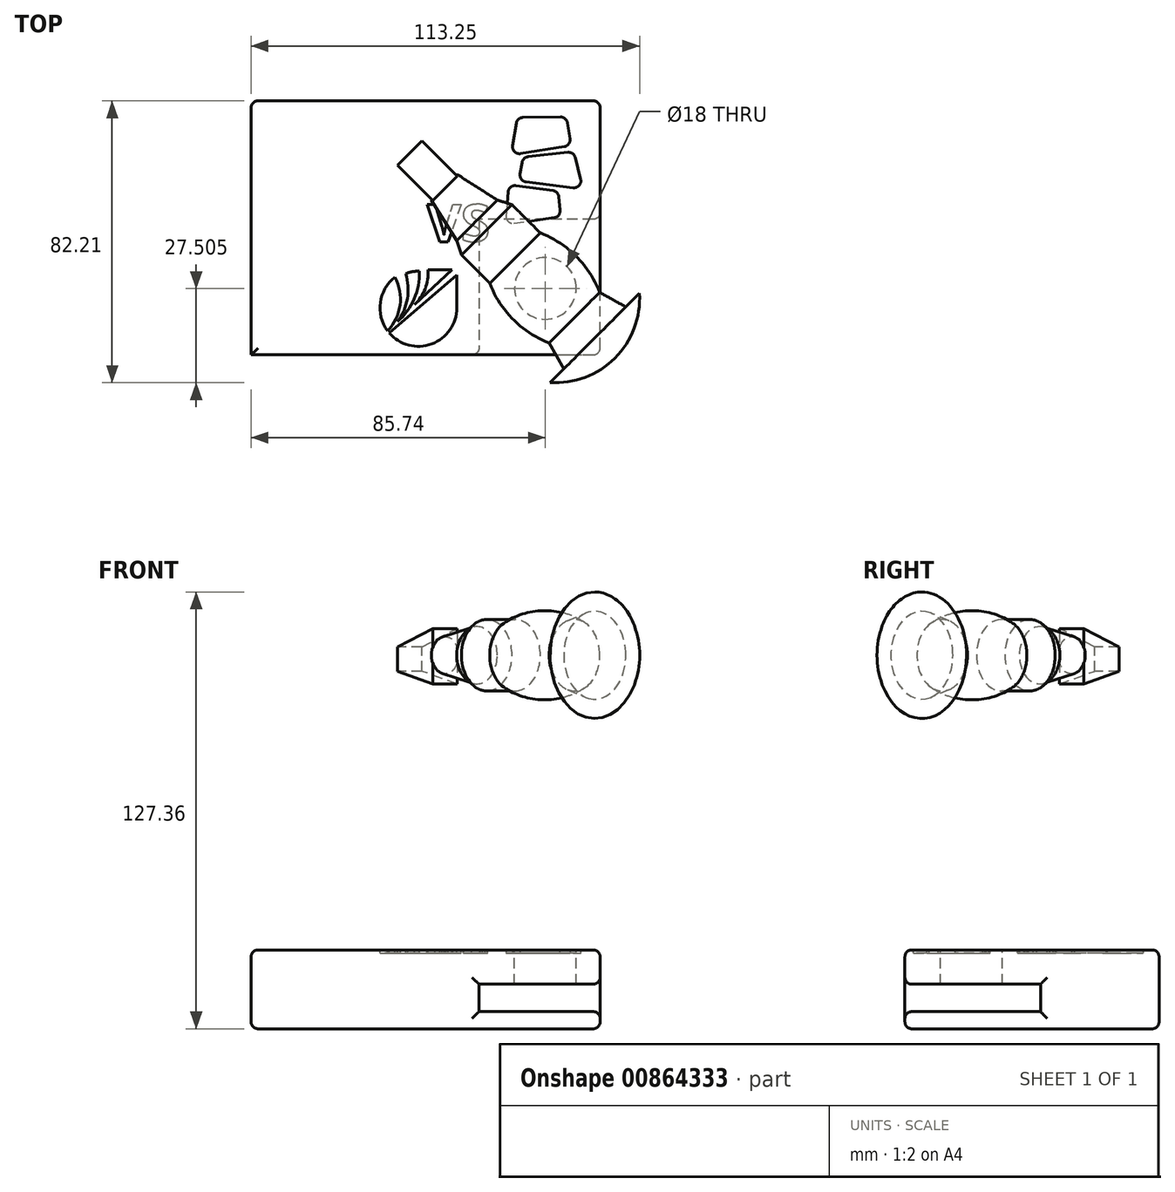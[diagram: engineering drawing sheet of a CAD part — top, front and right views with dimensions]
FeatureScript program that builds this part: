
annotation { "Feature Type Name" : "Feature", "Feature Type Description" : "" }
export const myFeature = defineFeature(function(context is Context, id is Id, definition is map)
    precondition{}
    {
        {
            var Q0;
            Q0=qCreatedBy(makeId("Top.planeOp"),FACE);
            cPlane(context, id + "F0", {"entities" : qUnion([Q0]), "cplaneType" : CPlaneType.OFFSET, "offset" : 36 * mm, "oppositeDirection" : true, "width" : 150 * mm, "height" : 150 * mm});
        }
        {
            var Q0;
            Q0=qCreatedBy(makeId("Top.planeOp"),FACE);
            cPlane(context, id + "F1", {"entities" : qUnion([Q0]), "cplaneType" : CPlaneType.OFFSET, "offset" : 40 * mm, "width" : 150 * mm, "height" : 150 * mm});
        }
        {
            var Q0;
            Q0=qCreatedBy(makeId("Front.planeOp"),FACE);
            var sketch = newSketch(context, id + "F2", { "sketchPlane" : qUnion([Q0])});
            skLineSegment(sketch, "E0", {"start": v(0, 86.74) * mm, "end": v(0, -86.44) * mm});
            skSolve(sketch);
        }
        {
            var Q0;
            Q0=sQuery(id+"F2.wireOp",EDGE,"E0");
            var Q1;
            Q1=qCreatedBy(makeId("Front.planeOp"),FACE);
            cPlane(context, id + "F3", {"entities" : qUnion([Q0, Q1]), "cplaneType" : CPlaneType.LINE_ANGLE, "offset" : 25 * mm, "angle" : 45 * degree, "width" : 150 * mm, "height" : 150 * mm});
        }
        {
            var Q0;
            Q0=qCreatedBy(id+"F3.planeOp",FACE);
            cPlane(context, id + "F4", {"entities" : qUnion([Q0]), "cplaneType" : CPlaneType.OFFSET, "offset" : 25 * mm, "width" : 150 * mm, "height" : 150 * mm});
        }
        {
            var Q0;
            Q0=qCreatedBy(id+"F4.planeOp",FACE);
            var sketch = newSketch(context, id + "F5", { "sketchPlane" : qUnion([Q0])});
            skLineSegment(sketch, "E1", {"start": v(-75.39, 49.92) * mm, "end": v(-11.92, 49.92) * mm});
            skLineSegment(sketch, "E2", {"start": v(-11.92, 49.92) * mm, "end": v(-11.92, 55.3) * mm});
            skLineSegment(sketch, "E3", {"start": v(-73.9, 62.7) * mm, "end": v(-73.9, 68.36) * mm});
            skLineSegment(sketch, "E4", {"start": v(-29.35, 60.33) * mm, "end": v(-41.03, 60.33) * mm});
            skArc(sketch, "E5", {"start": v(-41.03, 60.33) * mm, "mid": v(-53.27, 62.93) * mm, "end": v(-65.52, 60.33) * mm});
            skLineSegment(sketch, "E6", {"start": v(-65.52, 60.33) * mm, "end": v(-73.9, 62.7) * mm});
            skLineSegment(sketch, "E7", {"start": v(-11.92, 55.3) * mm, "end": v(-25.37, 58.26) * mm});
            skLineSegment(sketch, "E8", {"start": v(-25.37, 58.26) * mm, "end": v(-29.35, 60.33) * mm});
            skArc(sketch, "E9", {"start": v(-73.9, 68.36) * mm, "mid": v(-80.03, 60.03) * mm, "end": v(-82.2, 49.92) * mm});
            skLineSegment(sketch, "E10", {"start": v(-75.39, 49.92) * mm, "end": v(-82.2, 49.92) * mm});
            skSolve(sketch);
        }
        {
            var Q0;
            Q0=qSketchRegion(id+"F5",true);
            var Q1;
            Q1=sQuery(id+"F5.wireOp",EDGE,"E1");
            revolve(context, id + "F6", {"surfaceOperationType" : NewSurfaceOperationType.NEW, "entities" : qUnion([Q0]), "axis" : qUnion([Q1]), "revolveType" : RevolveType.FULL});
        }
        {
            var Q0;
            Q0=qCreatedBy(id+"F4.planeOp",FACE);
            var sketch = newSketch(context, id + "F7", { "sketchPlane" : qUnion([Q0])});
            skLineSegment(sketch, "E11", {"start": v(-12.2, 57.73) * mm, "end": v(-12.2, 41.5) * mm});
            skLineSegment(sketch, "E12", {"start": v(-12.2, 41.5) * mm, "end": v(2.33, 45.24) * mm});
            skLineSegment(sketch, "E13", {"start": v(2.33, 45.24) * mm, "end": v(2.33, 52.3) * mm});
            skLineSegment(sketch, "E14", {"start": v(2.33, 52.3) * mm, "end": v(-12.2, 57.73) * mm});
            skSolve(sketch);
        }
        {
            var Q0;
            Q0=qSketchRegion(id+"F7",true);
            extrude(context, id + "F8", {"entities" : qUnion([Q0]), "operationType" : NewBodyOperationType.ADD, "depth" : 5 * mm, "offsetDistance" : 25 * mm});
        }
        {
            var Q0;
            Q0=qSketchRegion(id+"F7",true);
            extrude(context, id + "F9", {"entities" : qUnion([Q0]), "operationType" : NewBodyOperationType.ADD, "oppositeDirection" : true, "depth" : 5 * mm, "offsetDistance" : 25 * mm});
        }
        {
            var Q0;
            Q0=qCreatedBy(id+"F0.planeOp",FACE);
            var sketch = newSketch(context, id + "F10", { "sketchPlane" : qUnion([Q0])});
            skCircle(sketch, "E15", {"center": v(55.51, -20.16) * mm, "radius": 7.65 * mm});
            skSolve(sketch);
        }
        {
            var Q0;
            Q0=qCreatedBy(id+"F0.planeOp",FACE);
            var sketch = newSketch(context, id + "F11", { "sketchPlane" : qUnion([Q0])});
            skLineSegment(sketch, "E16.bottom", {"start": v(-30.23, -39.51) * mm, "end": v(71.47, -39.51) * mm});
            skLineSegment(sketch, "E16.top", {"start": v(-30.23, 34.55) * mm, "end": v(71.47, 34.55) * mm});
            skLineSegment(sketch, "E16.left", {"start": v(-30.23, -39.51) * mm, "end": v(-30.23, 34.55) * mm});
            skLineSegment(sketch, "E16.right", {"start": v(71.47, -39.51) * mm, "end": v(71.47, 34.55) * mm});
            skCircle(sketch, "E17", {"center": v(55.51, -20.16) * mm, "radius": 9 * mm});
            skSolve(sketch);
        }
        {
            var Q0;
            Q0=qSketchRegion(id+"F11",true);
            extrude(context, id + "F12", {"entities" : qUnion([Q0]), "operationType" : NewBodyOperationType.ADD, "oppositeDirection" : true, "depth" : 10 * mm, "offsetDistance" : 25 * mm});
        }
        {
            var Q0;
            Q0=makeQuery(id+"F12.opExtrude","CAP_FACE",FACE,{"disambiguationData":[OSD([sQuery(id+"F11.wireOp",EDGE,"E16.bottom"),sQuery(id+"F11.wireOp",EDGE,"E16.top"),sQuery(id+"F11.wireOp",EDGE,"E16.left"),sQuery(id+"F11.wireOp",EDGE,"E16.right"),sQuery(id+"F11.wireOp",EDGE,"E17")])],"isStart":false});
            cPlane(context, id + "F13", {"entities" : qUnion([Q0]), "cplaneType" : CPlaneType.OFFSET, "offset" : 1 * mm, "width" : 150 * mm, "height" : 150 * mm});
        }
        {
            var Q0;
            Q0=makeQuery(id+"F12.opExtrude","CAP_FACE",FACE,{"disambiguationData":[OSD([sQuery(id+"F11.wireOp",EDGE,"E16.bottom"),sQuery(id+"F11.wireOp",EDGE,"E16.top"),sQuery(id+"F11.wireOp",EDGE,"E16.left"),sQuery(id+"F11.wireOp",EDGE,"E16.right"),sQuery(id+"F11.wireOp",EDGE,"E17")])],"isStart":false});
            var sketch = newSketch(context, id + "F14", { "sketchPlane" : qUnion([Q0])});
            skLineSegment(sketch, "E18", {"start": v(71.47, -34.55) * mm, "end": v(71.47, 0) * mm});
            skLineSegment(sketch, "E19", {"start": v(71.47, 0) * mm, "end": v(36.17, 0) * mm});
            skLineSegment(sketch, "E20", {"start": v(-30.23, -34.55) * mm, "end": v(71.47, -34.55) * mm});
            skLineSegment(sketch, "E21", {"start": v(-30.23, -34.55) * mm, "end": v(-30.23, 0) * mm});
            skLineSegment(sketch, "E22", {"start": v(36.17, 0) * mm, "end": v(36.17, 39.51) * mm});
            skLineSegment(sketch, "E23", {"start": v(36.17, 39.51) * mm, "end": v(-30.23, 39.51) * mm});
            skLineSegment(sketch, "E24", {"start": v(-30.23, 39.51) * mm, "end": v(-30.23, 0) * mm});
            skSolve(sketch);
        }
        {
            var Q0;
            Q0=makeQuery(id+"F14.imprint","IMPRINT",FACE,{"disambiguationData":[TD([[makeQuery(id+"F14.imprint","IMPRINT",EDGE,{"derivedFrom":sQuery(id+"F14.wireOp",EDGE,"E18")}),-1.0]])]});
            extrude(context, id + "F15", {"entities" : qUnion([Q0]), "operationType" : NewBodyOperationType.ADD, "depth" : 8 * mm, "offsetDistance" : 25 * mm});
        }
        {
            var Q0;
            Q0=makeQuery(id+"F15.opExtrude","CAP_FACE",FACE,{"disambiguationData":[OSD([sQuery(id+"F14.wireOp",EDGE,"E18"),sQuery(id+"F14.wireOp",EDGE,"E19"),sQuery(id+"F14.wireOp",EDGE,"E20"),sQuery(id+"F14.wireOp",EDGE,"iN0juFn1-ICa9-M7KA-fJVA-QljqQybucplU"),sQuery(id+"F14.wireOp",EDGE,"E21")])],"isStart":false});
            var sketch = newSketch(context, id + "F16", { "sketchPlane" : qUnion([Q0])});
            skLineSegment(sketch, "E25.bottom", {"start": v(-30.23, -34.55) * mm, "end": v(71.47, -34.55) * mm});
            skLineSegment(sketch, "E25.top", {"start": v(-30.23, 39.51) * mm, "end": v(71.47, 39.51) * mm});
            skLineSegment(sketch, "E25.left", {"start": v(-30.23, -34.55) * mm, "end": v(-30.23, 39.51) * mm});
            skLineSegment(sketch, "E25.right", {"start": v(71.47, -34.55) * mm, "end": v(71.47, 39.51) * mm});
            skSolve(sketch);
        }
        {
            var Q0;
            Q0=qSketchRegion(id+"F16",true);
            extrude(context, id + "F17", {"entities" : qUnion([Q0]), "operationType" : NewBodyOperationType.ADD, "depth" : 5 * mm, "offsetDistance" : 25 * mm});
        }
        {
            var Q0;
            Q0=makeQuery(id+"F12.opExtrude","CAP_FACE",FACE,{"disambiguationData":[OSD([sQuery(id+"F11.wireOp",EDGE,"E16.bottom"),sQuery(id+"F11.wireOp",EDGE,"E16.top"),sQuery(id+"F11.wireOp",EDGE,"E16.left"),sQuery(id+"F11.wireOp",EDGE,"E16.right"),sQuery(id+"F11.wireOp",EDGE,"E17")])],"isStart":true});
            var sketch = newSketch(context, id + "F18", { "sketchPlane" : qUnion([Q0])});
            skLineSegment(sketch, "E26.bottom", {"start": v(65.5, -22.08) * mm, "end": v(62.22, -22.08) * mm});
            skLineSegment(sketch, "E26.top", {"start": v(65.5, -21.47) * mm, "end": v(62.22, -21.47) * mm});
            skLineSegment(sketch, "E26.left", {"start": v(65.5, -22.08) * mm, "end": v(65.5, -21.47) * mm});
            skLineSegment(sketch, "E26.right", {"start": v(62.22, -22.08) * mm, "end": v(62.22, -21.47) * mm});
            skSolve(sketch);
        }
        {
            var Q0;
            Q0=makeQuery(id+"FpY5HfDL9gUgUrJ_86.boolean.opBoolean","MERGE",FACE,{"derivedFrom":[makeQuery(id+"F12.opExtrude","CAP_FACE",FACE,{"disambiguationData":[OSD([sQuery(id+"F11.wireOp",EDGE,"E16.bottom"),sQuery(id+"F11.wireOp",EDGE,"E16.top"),sQuery(id+"F11.wireOp",EDGE,"E16.left"),sQuery(id+"F11.wireOp",EDGE,"E16.right"),sQuery(id+"F11.wireOp",EDGE,"E17")])],"isStart":true}),makeQuery(id+"FpY5HfDL9gUgUrJ_86.opExtrude","CAP_FACE",FACE,{"disambiguationData":[OSD([sQuery(id+"F18.wireOp",EDGE,"E26.bottom"),sQuery(id+"F18.wireOp",EDGE,"E26.top"),sQuery(id+"F18.wireOp",EDGE,"E26.left"),sQuery(id+"F18.wireOp",EDGE,"E26.right")])],"isStart":true})]});
            var sketch = newSketch(context, id + "F19", { "sketchPlane" : qUnion([Q0])});
            skLineSegment(sketch, "E27", {"start": v(47.35, 29.69) * mm, "end": v(45.56, 18.71) * mm});
            skLineSegment(sketch, "E28", {"start": v(45.56, 18.71) * mm, "end": v(63, 21.5) * mm});
            skLineSegment(sketch, "E29", {"start": v(63, 21.5) * mm, "end": v(61.68, 29.86) * mm});
            skLineSegment(sketch, "E30", {"start": v(61.68, 29.86) * mm, "end": v(47.35, 29.69) * mm});
            skLineSegment(sketch, "E31", {"start": v(48.97, 18.09) * mm, "end": v(47.85, 11.15) * mm});
            skLineSegment(sketch, "E32", {"start": v(47.85, 11.15) * mm, "end": v(66.52, 8.87) * mm});
            skLineSegment(sketch, "E33", {"start": v(63.83, 19.72) * mm, "end": v(48.97, 18.09) * mm});
            skLineSegment(sketch, "E34", {"start": v(63.83, 19.72) * mm, "end": v(66.52, 8.87) * mm});
            skLineSegment(sketch, "E35", {"start": v(44.9, 10.13) * mm, "end": v(43.84, -1.5) * mm});
            skLineSegment(sketch, "E36", {"start": v(43.84, -1.5) * mm, "end": v(59.99, 0.74) * mm});
            skLineSegment(sketch, "E37", {"start": v(59.3, 8.18) * mm, "end": v(44.9, 10.13) * mm});
            skLineSegment(sketch, "E38", {"start": v(59.3, 8.18) * mm, "end": v(59.99, 0.74) * mm});
            skSolve(sketch);
        }
        {
            var Q0;
            Q0=qSketchRegion(id+"F19",true);
            extrude(context, id + "F20", {"entities" : qUnion([Q0]), "operationType" : NewBodyOperationType.REMOVE, "oppositeDirection" : true, "depth" : 1 * mm, "offsetDistance" : 25 * mm});
        }
        {
            var Q0;
            Q0=makeQuery(id+"F20.boolean.opBoolean","COPY",EDGE,{"derivedFrom":makeQuery(id+"F20.opExtrude","SWEPT_EDGE",EDGE,{"disambiguationData":[OSD([sQuery(id+"F19.wireOp",EDGE,"E36"),sQuery(id+"F19.wireOp",EDGE,"E38")])]})});
            var Q1;
            Q1=makeQuery(id+"F20.boolean.opBoolean","COPY",EDGE,{"derivedFrom":makeQuery(id+"F20.opExtrude","SWEPT_EDGE",EDGE,{"disambiguationData":[OSD([sQuery(id+"F19.wireOp",EDGE,"E37"),sQuery(id+"F19.wireOp",EDGE,"E38")])]})});
            var Q2;
            Q2=makeQuery(id+"F20.boolean.opBoolean","COPY",EDGE,{"derivedFrom":makeQuery(id+"F20.opExtrude","SWEPT_EDGE",EDGE,{"disambiguationData":[OSD([sQuery(id+"F19.wireOp",EDGE,"E35"),sQuery(id+"F19.wireOp",EDGE,"E36")])]})});
            var Q3;
            Q3=makeQuery(id+"F20.boolean.opBoolean","COPY",EDGE,{"derivedFrom":makeQuery(id+"F20.opExtrude","SWEPT_EDGE",EDGE,{"disambiguationData":[OSD([sQuery(id+"F19.wireOp",EDGE,"E35"),sQuery(id+"F19.wireOp",EDGE,"E37")])]})});
            var Q4;
            Q4=makeQuery(id+"F20.boolean.opBoolean","COPY",EDGE,{"derivedFrom":makeQuery(id+"F20.opExtrude","SWEPT_EDGE",EDGE,{"disambiguationData":[OSD([sQuery(id+"F19.wireOp",EDGE,"E31"),sQuery(id+"F19.wireOp",EDGE,"E32")])]})});
            var Q5;
            Q5=makeQuery(id+"F20.boolean.opBoolean","COPY",EDGE,{"derivedFrom":makeQuery(id+"F20.opExtrude","SWEPT_EDGE",EDGE,{"disambiguationData":[OSD([sQuery(id+"F19.wireOp",EDGE,"E27"),sQuery(id+"F19.wireOp",EDGE,"E28")])]})});
            var Q6;
            Q6=makeQuery(id+"F20.boolean.opBoolean","COPY",EDGE,{"derivedFrom":makeQuery(id+"F20.opExtrude","SWEPT_EDGE",EDGE,{"disambiguationData":[OSD([sQuery(id+"F19.wireOp",EDGE,"E31"),sQuery(id+"F19.wireOp",EDGE,"E33")])]})});
            var Q7;
            Q7=makeQuery(id+"F20.boolean.opBoolean","COPY",EDGE,{"derivedFrom":makeQuery(id+"F20.opExtrude","SWEPT_EDGE",EDGE,{"disambiguationData":[OSD([sQuery(id+"F19.wireOp",EDGE,"E27"),sQuery(id+"F19.wireOp",EDGE,"E30")])]})});
            var Q8;
            Q8=makeQuery(id+"F20.boolean.opBoolean","COPY",EDGE,{"derivedFrom":makeQuery(id+"F20.opExtrude","SWEPT_EDGE",EDGE,{"disambiguationData":[OSD([sQuery(id+"F19.wireOp",EDGE,"E29"),sQuery(id+"F19.wireOp",EDGE,"E30")])]})});
            var Q9;
            Q9=makeQuery(id+"F20.boolean.opBoolean","COPY",EDGE,{"derivedFrom":makeQuery(id+"F20.opExtrude","SWEPT_EDGE",EDGE,{"disambiguationData":[OSD([sQuery(id+"F19.wireOp",EDGE,"E33"),sQuery(id+"F19.wireOp",EDGE,"E34")])]})});
            var Q10;
            Q10=makeQuery(id+"F20.boolean.opBoolean","COPY",EDGE,{"derivedFrom":makeQuery(id+"F20.opExtrude","SWEPT_EDGE",EDGE,{"disambiguationData":[OSD([sQuery(id+"F19.wireOp",EDGE,"E28"),sQuery(id+"F19.wireOp",EDGE,"E29")])]})});
            var Q11;
            Q11=makeQuery(id+"F20.boolean.opBoolean","COPY",EDGE,{"derivedFrom":makeQuery(id+"F20.opExtrude","SWEPT_EDGE",EDGE,{"disambiguationData":[OSD([sQuery(id+"F19.wireOp",EDGE,"E32"),sQuery(id+"F19.wireOp",EDGE,"E34")])]})});
            fillet(context, id + "F21", {"entities" : qUnion([Q0, Q1, Q2, Q3, Q4, Q5, Q6, Q7, Q8, Q9, Q10, Q11]), "radius" : 2 * mm, "tangentPropagation" : true, "allowEdgeOverflow" : false});
        }
        {
            var Q0;
            Q0=makeQuery(id+"FpY5HfDL9gUgUrJ_86.boolean.opBoolean","MERGE",FACE,{"derivedFrom":[makeQuery(id+"F12.opExtrude","CAP_FACE",FACE,{"disambiguationData":[OSD([sQuery(id+"F11.wireOp",EDGE,"E16.bottom"),sQuery(id+"F11.wireOp",EDGE,"E16.top"),sQuery(id+"F11.wireOp",EDGE,"E16.left"),sQuery(id+"F11.wireOp",EDGE,"E16.right"),sQuery(id+"F11.wireOp",EDGE,"E17")])],"isStart":true}),makeQuery(id+"FpY5HfDL9gUgUrJ_86.opExtrude","CAP_FACE",FACE,{"disambiguationData":[OSD([sQuery(id+"F18.wireOp",EDGE,"E26.bottom"),sQuery(id+"F18.wireOp",EDGE,"E26.top"),sQuery(id+"F18.wireOp",EDGE,"E26.left"),sQuery(id+"F18.wireOp",EDGE,"E26.right")])],"isStart":true})]});
            var sketch = newSketch(context, id + "F22", { "sketchPlane" : qUnion([Q0])});
            skArc(sketch, "E39", {"start": v(10.01, -33.1) * mm, "mid": v(22.42, -36.32) * mm, "end": v(29.75, -25.8) * mm});
            skLineSegment(sketch, "E40", {"start": v(29.75, -25.8) * mm, "end": v(29.75, -16.19) * mm});
            skLineSegment(sketch, "E41", {"start": v(29.75, -16.19) * mm, "end": v(18.53, -25.8) * mm});
            skLineSegment(sketch, "E42", {"start": v(10.01, -33.1) * mm, "end": v(18.53, -25.8) * mm});
            skLineSegment(sketch, "E43", {"start": v(28.26, -14.71) * mm, "end": v(21.29, -14.71) * mm});
            skLineSegment(sketch, "E44", {"start": v(28.26, -14.71) * mm, "end": v(17.39, -24.9) * mm});
            skArc(sketch, "E45", {"start": v(11.71, -16.9) * mm, "mid": v(7.42, -24.24) * mm, "end": v(9.53, -32.5) * mm});
            skArc(sketch, "E46", {"start": v(9.53, -32.5) * mm, "mid": v(13.18, -25.05) * mm, "end": v(11.71, -16.9) * mm});
            skArc(sketch, "E47", {"start": v(12.42, -29.83) * mm, "mid": v(15.32, -23.1) * mm, "end": v(14.8, -15.79) * mm});
            skArc(sketch, "E48", {"start": v(12.42, -29.83) * mm, "mid": v(17.27, -23.2) * mm, "end": v(18.83, -15.12) * mm});
            skArc(sketch, "E49", {"start": v(17.39, -24.9) * mm, "mid": v(20.5, -20.25) * mm, "end": v(21.29, -14.71) * mm});
            skArc(sketch, "E50", {"start": v(18.83, -15.12) * mm, "mid": v(16.78, -15.26) * mm, "end": v(14.8, -15.79) * mm});
            skText(sketch, "E51", { "text": "VS", "fontName": "OpenSans-Bold.ttf"});
            const initialGuessF22  = {"E51": [0.02102, -0.00654, 1, 0, 0.01097]};
            skSetInitialGuess(sketch, initialGuessF22);
            skSolve(sketch);
        }
        {
            var Q0;
            Q0=qSketchRegion(id+"F22",true);
            extrude(context, id + "F23", {"entities" : qUnion([Q0]), "operationType" : NewBodyOperationType.REMOVE, "oppositeDirection" : true, "depth" : 1 * mm, "offsetDistance" : 25 * mm});
        }
        {
            var Q0;
            Q0=makeQuery(id+"F12.opExtrude","CAP_EDGE",EDGE,{"disambiguationData":[OSD([sQuery(id+"F11.wireOp",EDGE,"E16.bottom")])],"isStart":true});
            var Q1;
            Q1=makeQuery(id+"F12.opExtrude","CAP_EDGE",EDGE,{"disambiguationData":[OSD([sQuery(id+"F11.wireOp",EDGE,"E16.right")])],"isStart":true});
            var Q2;
            Q2=makeQuery(id+"F12.opExtrude","SWEPT_EDGE",EDGE,{"disambiguationData":[OSD([sQuery(id+"F11.wireOp",EDGE,"E16.bottom"),sQuery(id+"F11.wireOp",EDGE,"E16.right")])]});
            var Q3;
            Q3=makeQuery(id+"F17.opExtrude","SWEPT_EDGE",EDGE,{"disambiguationData":[OSD([sQuery(id+"F16.wireOp",EDGE,"E25.top"),sQuery(id+"F16.wireOp",EDGE,"E25.right")])]});
            var Q4;
            Q4=makeQuery(id+"F17.opExtrude","CAP_EDGE",EDGE,{"disambiguationData":[OSD([sQuery(id+"F16.wireOp",EDGE,"E25.top")])],"isStart":true});
            var Q5;
            Q5=makeQuery(id+"F17.opExtrude","CAP_EDGE",EDGE,{"disambiguationData":[OSD([sQuery(id+"F16.wireOp",EDGE,"E25.right")])],"isStart":true});
            var Q6;
            Q6=makeQuery(id+"F15.opExtrude","SWEPT_EDGE",EDGE,{"disambiguationData":[OSD([sQuery(id+"F11.wireOp",EDGE,"E16.right"),sQuery(id+"F14.wireOp",EDGE,"E18"),sQuery(id+"F14.wireOp",EDGE,"E19")])]});
            var Q7;
            Q7=makeQuery(id+"F12.opExtrude","CAP_EDGE",EDGE,{"disambiguationData":[OSD([sQuery(id+"F11.wireOp",EDGE,"E16.right")])],"isStart":false});
            var Q8;
            Q8=makeQuery(id+"F12.opExtrude","CAP_EDGE",EDGE,{"disambiguationData":[OSD([sQuery(id+"F11.wireOp",EDGE,"E16.bottom")])],"isStart":false});
            var Q9;
            Q9=makeQuery(id+"F15.opExtrude","SWEPT_EDGE",EDGE,{"disambiguationData":[OSD([sQuery(id+"F11.wireOp",EDGE,"E16.bottom"),sQuery(id+"F14.wireOp",EDGE,"E22"),sQuery(id+"F14.wireOp",EDGE,"E23")])]});
            var Q10;
            Q10=makeQuery(id+"F17.opExtrude","CAP_EDGE",EDGE,{"disambiguationData":[OSD([sQuery(id+"F16.wireOp",EDGE,"E25.top")])],"isStart":false});
            var Q11;
            Q11=makeQuery(id+"F17.opExtrude","CAP_EDGE",EDGE,{"disambiguationData":[OSD([sQuery(id+"F16.wireOp",EDGE,"E25.right")])],"isStart":false});
            var Q12;
            Q12=makeQuery(id+"F17.opExtrude","CAP_EDGE",EDGE,{"disambiguationData":[OSD([sQuery(id+"F16.wireOp",EDGE,"E25.bottom")])],"isStart":false});
            var Q13;
            Q13=makeQuery(id+"F17.boolean.opBoolean","MERGE",EDGE,{"derivedFrom":[makeQuery(id+"F15.boolean.opBoolean","MERGE",EDGE,{"derivedFrom":[makeQuery(id+"F12.opExtrude","SWEPT_EDGE",EDGE,{"disambiguationData":[OSD([sQuery(id+"F11.wireOp",EDGE,"E16.top"),sQuery(id+"F11.wireOp",EDGE,"E16.right")])]}),makeQuery(id+"F15.opExtrude","SWEPT_EDGE",EDGE,{"disambiguationData":[OSD([sQuery(id+"F14.wireOp",EDGE,"E18"),sQuery(id+"F14.wireOp",EDGE,"E20")])]})]}),makeQuery(id+"F17.opExtrude","SWEPT_EDGE",EDGE,{"disambiguationData":[OSD([sQuery(id+"F16.wireOp",EDGE,"E25.bottom"),sQuery(id+"F16.wireOp",EDGE,"E25.right")])]})]});
            var Q14;
            Q14=makeQuery(id+"F17.boolean.opBoolean","MERGE",EDGE,{"derivedFrom":[makeQuery(id+"F15.boolean.opBoolean","MERGE",EDGE,{"derivedFrom":[makeQuery(id+"F12.opExtrude","SWEPT_EDGE",EDGE,{"disambiguationData":[OSD([sQuery(id+"F11.wireOp",EDGE,"E16.top"),sQuery(id+"F11.wireOp",EDGE,"E16.left")])]}),makeQuery(id+"F15.opExtrude","SWEPT_EDGE",EDGE,{"disambiguationData":[OSD([sQuery(id+"F14.wireOp",EDGE,"E20"),sQuery(id+"F14.wireOp",EDGE,"E21")])]})]}),makeQuery(id+"F17.opExtrude","SWEPT_EDGE",EDGE,{"disambiguationData":[OSD([sQuery(id+"F16.wireOp",EDGE,"E25.bottom"),sQuery(id+"F16.wireOp",EDGE,"E25.left")])]})]});
            var Q15;
            Q15=makeQuery(id+"F12.opExtrude","CAP_EDGE",EDGE,{"disambiguationData":[OSD([sQuery(id+"F11.wireOp",EDGE,"E16.top")])],"isStart":true});
            var Q16;
            Q16=makeQuery(id+"F17.opExtrude","CAP_FACE",FACE,{"disambiguationData":[OSD([sQuery(id+"F16.wireOp",EDGE,"E25.bottom"),sQuery(id+"F16.wireOp",EDGE,"E25.top"),sQuery(id+"F16.wireOp",EDGE,"E25.left"),sQuery(id+"F16.wireOp",EDGE,"E25.right")])],"isStart":false});
            var Q17;
            Q17=makeQuery(id+"F12.opExtrude","CAP_EDGE",EDGE,{"disambiguationData":[OSD([sQuery(id+"F11.wireOp",EDGE,"E16.left")])],"isStart":true});
            fillet(context, id + "F24", {"entities" : qUnion([Q0, Q1, Q2, Q3, Q4, Q5, Q6, Q7, Q8, Q9, Q10, Q11, Q12, Q13, Q14, Q15, Q16, Q17]), "radius" : 2 * mm, "tangentPropagation" : true, "allowEdgeOverflow" : false});
        }
    });
